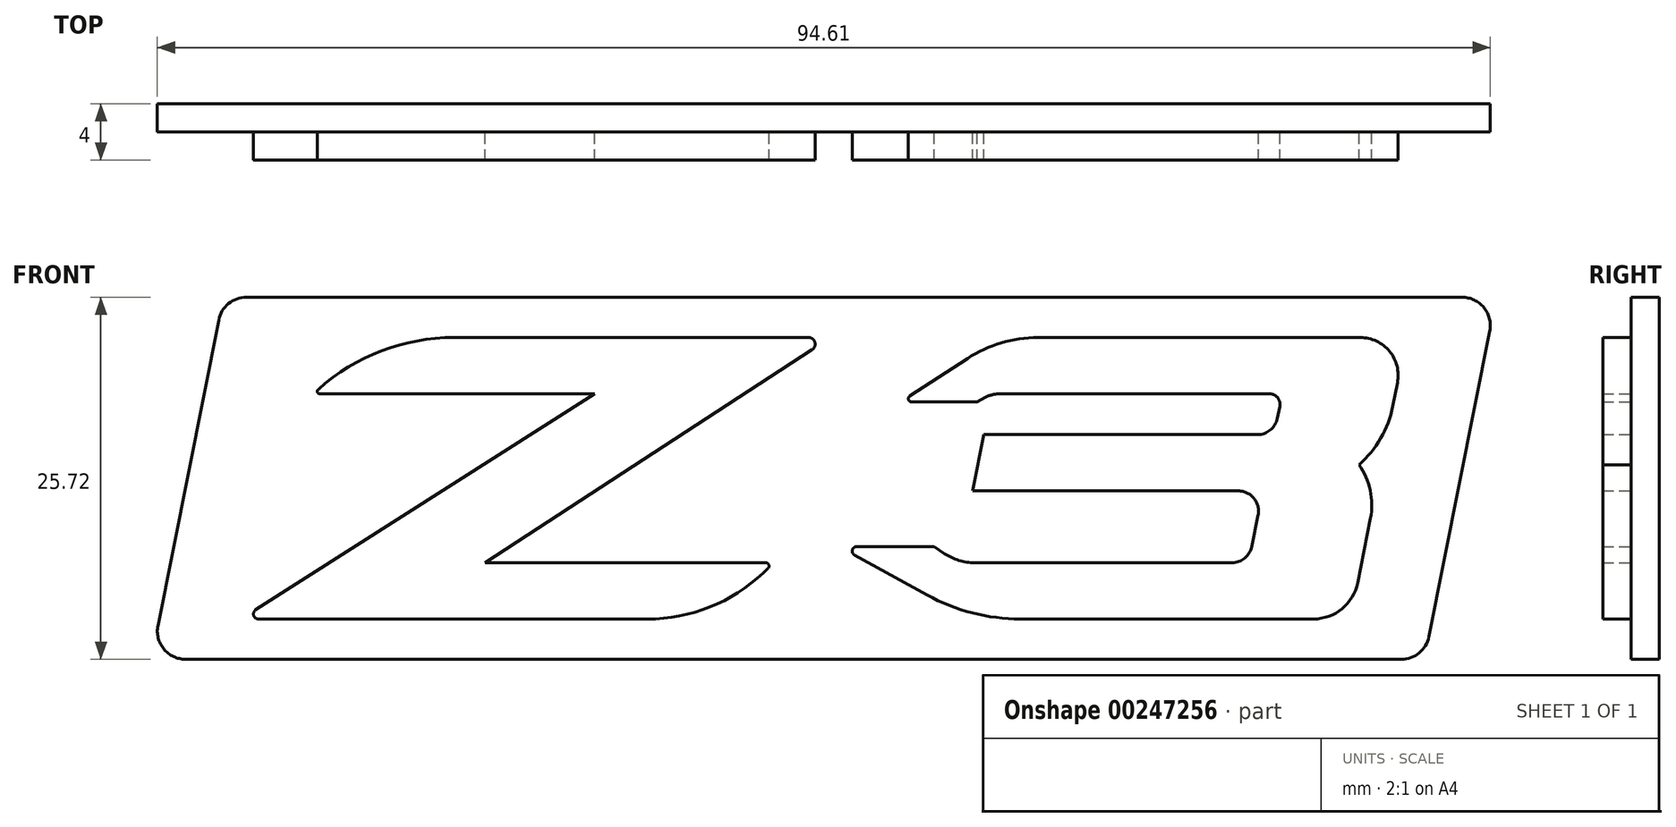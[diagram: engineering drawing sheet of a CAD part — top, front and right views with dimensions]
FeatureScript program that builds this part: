
annotation { "Feature Type Name" : "Feature", "Feature Type Description" : "" }
export const myFeature = defineFeature(function(context is Context, id is Id, definition is map)
    precondition{}
    {
        {
            var Q0;
            Q0=qCreatedBy(makeId("Front.planeOp"),FACE);
            var sketch = newSketch(context, id + "F0", { "sketchPlane" : qUnion([Q0])});
            skLineSegment(sketch, "E0", {"start": v(-146.44, 42.92) * mm, "end": v(151.69, 42.92) * mm, "construction": true});
            skLineSegment(sketch, "E1", {"start": v(-146.44, -27.08) * mm, "end": v(151.69, -27.08) * mm, "construction": true});
            skLineSegment(sketch, "E2", {"start": v(-146.44, 28.92) * mm, "end": v(151.69, 28.92) * mm, "construction": true});
            skLineSegment(sketch, "E3", {"start": v(-146.44, -13.08) * mm, "end": v(131.87, -13.08) * mm, "construction": true});
            skLineSegment(sketch, "E4", {"start": v(-142.86, -24.8) * mm, "end": v(-58.68, 28.92) * mm});
            skLineSegment(sketch, "E5", {"start": v(-58.68, 28.92) * mm, "end": v(-126.94, 28.92) * mm});
            skLineSegment(sketch, "E6", {"start": v(-127.34, 29.98) * mm, "end": v(-127.28, 30.04) * mm});
            skLineSegment(sketch, "E7", {"start": v(-93.58, 42.92) * mm, "end": v(-5.53, 42.92) * mm});
            skLineSegment(sketch, "E8", {"start": v(-4.63, 39.9) * mm, "end": v(-85.86, -13.08) * mm});
            skLineSegment(sketch, "E9", {"start": v(-85.86, -13.08) * mm, "end": v(-16.17, -13.08) * mm});
            skLineSegment(sketch, "E10", {"start": v(-15.6, -14.51) * mm, "end": v(-16.8, -15.65) * mm});
            skLineSegment(sketch, "E11", {"start": v(-45.51, -27.08) * mm, "end": v(-142.2, -27.08) * mm});
            skLineSegment(sketch, "E12", {"start": v(41.87, 28.92) * mm, "end": v(106.05, 28.92) * mm});
            skLineSegment(sketch, "E13", {"start": v(99.7, -13.08) * mm, "end": v(35.77, -13.08) * mm});
            skLineSegment(sketch, "E14", {"start": v(110.12, 18.76) * mm, "end": v(107.34, 4.76) * mm, "construction": true});
            skLineSegment(sketch, "E15", {"start": v(106.15, -1.2) * mm, "end": v(104.6, -9.06) * mm});
            skLineSegment(sketch, "E16", {"start": v(106.02, 18.76) * mm, "end": v(38, 18.76) * mm});
            skLineSegment(sketch, "E17", {"start": v(38, 18.76) * mm, "end": v(35.22, 4.76) * mm});
            skLineSegment(sketch, "E18", {"start": v(35.22, 4.76) * mm, "end": v(101.25, 4.76) * mm});
            skLineSegment(sketch, "E19", {"start": v(33.98, 37.72) * mm, "end": v(19.62, 28.35) * mm});
            skLineSegment(sketch, "E20", {"start": v(20.05, 26.92) * mm, "end": v(36.32, 26.92) * mm});
            skLineSegment(sketch, "E21", {"start": v(36.32, 26.92) * mm, "end": v(38.4, 28.04) * mm});
            skLineSegment(sketch, "E22", {"start": v(38, 18.76) * mm, "end": v(42.8, 42.92) * mm, "construction": true});
            skLineSegment(sketch, "E23", {"start": v(130.88, -18.05) * mm, "end": v(131.87, -13.08) * mm});
            skLineSegment(sketch, "E24", {"start": v(51.48, 42.92) * mm, "end": v(131.57, 42.92) * mm});
            skLineSegment(sketch, "E25", {"start": v(119.88, -27.08) * mm, "end": v(47.15, -27.08) * mm});
            skLineSegment(sketch, "E26", {"start": v(23.92, -21.1) * mm, "end": v(5.88, -11.14) * mm});
            skLineSegment(sketch, "E27", {"start": v(6.41, -9.08) * mm, "end": v(25.65, -9.08) * mm});
            skLineSegment(sketch, "E28", {"start": v(25.65, -9.08) * mm, "end": v(28.27, -10.82) * mm});
            skLineSegment(sketch, "E29", {"start": v(35.22, 4.76) * mm, "end": v(31.68, -13.08) * mm, "construction": true});
            skLineSegment(sketch, "E30", {"start": v(131.87, -13.08) * mm, "end": v(151.69, -13.08) * mm, "construction": true});
            skLineSegment(sketch, "E31", {"start": v(140.22, 28.92) * mm, "end": v(140.77, 31.7) * mm});
            skLineSegment(sketch, "E32", {"start": v(131.87, -13.08) * mm, "end": v(140.22, 28.92) * mm, "construction": true});
            skLineSegment(sketch, "E33", {"start": v(131.87, -13.08) * mm, "end": v(134.06, -2.07) * mm});
            skLineSegment(sketch, "E34", {"start": v(116.96, 18.76) * mm, "end": v(110.12, 18.76) * mm, "construction": true});
            skPoint(sketch, "E35.visualSharp", {"position": v(138.2, 18.76) * mm});
            skArc(sketch, "E35.filletArc", {"start": v(134.06, -2.07) * mm, "mid": v(134.02, 4.9) * mm, "end": v(131.26, 11.3) * mm});
            skLineSegment(sketch, "E36", {"start": v(140.22, 28.92) * mm, "end": v(139.6, 25.8) * mm});
            skLineSegment(sketch, "E37", {"start": v(113.97, 4.76) * mm, "end": v(107.34, 4.76) * mm, "construction": true});
            skPoint(sketch, "E38.visualSharp", {"position": v(135.42, 4.76) * mm});
            skArc(sketch, "E38.filletArc", {"start": v(113.97, 4.76) * mm, "mid": v(123.21, 6.45) * mm, "end": v(131.26, 11.3) * mm, "construction": true});
            skArc(sketch, "E39", {"start": v(131.26, 11.3) * mm, "mid": v(125.02, 16.79) * mm, "end": v(116.96, 18.76) * mm, "construction": true});
            skArc(sketch, "E40", {"start": v(131.26, 11.3) * mm, "mid": v(136.62, 17.87) * mm, "end": v(139.6, 25.8) * mm});
            skPoint(sketch, "E41.visualSharp", {"position": v(110.12, 18.76) * mm});
            skArc(sketch, "E41.filletArc", {"start": v(106.02, 18.76) * mm, "mid": v(109.2, 19.9) * mm, "end": v(110.92, 22.8) * mm});
            skPoint(sketch, "E42.visualSharp", {"position": v(107.34, 4.76) * mm});
            skArc(sketch, "E42.filletArc", {"start": v(106.15, -1.2) * mm, "mid": v(105.11, 2.94) * mm, "end": v(101.25, 4.76) * mm});
            skPoint(sketch, "E43.visualSharp", {"position": v(103.8, -13.08) * mm});
            skArc(sketch, "E43.filletArc", {"start": v(99.7, -13.08) * mm, "mid": v(102.86, -11.95) * mm, "end": v(104.6, -9.06) * mm});
            skPoint(sketch, "E44.visualSharp", {"position": v(143, 42.92) * mm});
            skArc(sketch, "E44.filletArc", {"start": v(140.77, 31.7) * mm, "mid": v(138.82, 39.49) * mm, "end": v(131.57, 42.92) * mm});
            skPoint(sketch, "E45.visualSharp", {"position": v(129.09, -27.08) * mm});
            skArc(sketch, "E45.filletArc", {"start": v(119.88, -27.08) * mm, "mid": v(127, -24.54) * mm, "end": v(130.88, -18.05) * mm});
            skPoint(sketch, "E46.visualSharp", {"position": v(34.76, -27.08) * mm});
            skArc(sketch, "E46.filletArc", {"start": v(23.92, -21.1) * mm, "mid": v(35.15, -25.56) * mm, "end": v(47.15, -27.08) * mm});
            skPoint(sketch, "E47.visualSharp", {"position": v(2.16, -9.08) * mm});
            skArc(sketch, "E47.filletArc", {"start": v(6.41, -9.08) * mm, "mid": v(5.35, -9.9) * mm, "end": v(5.88, -11.14) * mm});
            skPoint(sketch, "E48.visualSharp", {"position": v(31.68, -13.08) * mm});
            skArc(sketch, "E48.filletArc", {"start": v(28.27, -10.82) * mm, "mid": v(31.85, -12.5) * mm, "end": v(35.77, -13.08) * mm});
            skPoint(sketch, "E49.visualSharp", {"position": v(40.02, 28.92) * mm});
            skArc(sketch, "E49.filletArc", {"start": v(41.87, 28.92) * mm, "mid": v(40.08, 28.7) * mm, "end": v(38.4, 28.04) * mm});
            skPoint(sketch, "E50.visualSharp", {"position": v(17.42, 26.92) * mm});
            skArc(sketch, "E50.filletArc", {"start": v(19.62, 28.35) * mm, "mid": v(19.3, 27.47) * mm, "end": v(20.05, 26.92) * mm});
            skPoint(sketch, "E51.visualSharp", {"position": v(0, 42.92) * mm});
            skArc(sketch, "E51.filletArc", {"start": v(-4.63, 39.9) * mm, "mid": v(-3.95, 41.74) * mm, "end": v(-5.53, 42.92) * mm});
            skPoint(sketch, "E52.visualSharp", {"position": v(-28.88, -27.08) * mm});
            skArc(sketch, "E52.filletArc", {"start": v(-45.51, -27.08) * mm, "mid": v(-30.06, -24.12) * mm, "end": v(-16.8, -15.65) * mm});
            skPoint(sketch, "E53.visualSharp", {"position": v(-14.1, -13.08) * mm});
            skArc(sketch, "E53.filletArc", {"start": v(-15.6, -14.51) * mm, "mid": v(-15.4, -13.6) * mm, "end": v(-16.17, -13.08) * mm});
            skPoint(sketch, "E54.visualSharp", {"position": v(-146.44, -27.08) * mm});
            skArc(sketch, "E54.filletArc", {"start": v(-142.86, -24.8) * mm, "mid": v(-143.39, -26.2) * mm, "end": v(-142.2, -27.08) * mm});
            skPoint(sketch, "E55.visualSharp", {"position": v(-112.89, 42.92) * mm});
            skArc(sketch, "E55.filletArc", {"start": v(-93.58, 42.92) * mm, "mid": v(-111.62, 39.59) * mm, "end": v(-127.28, 30.04) * mm});
            skPoint(sketch, "E56.visualSharp", {"position": v(-128.53, 28.92) * mm});
            skArc(sketch, "E56.filletArc", {"start": v(-127.34, 29.98) * mm, "mid": v(-127.5, 29.3) * mm, "end": v(-126.94, 28.92) * mm});
            skLineSegment(sketch, "E57", {"start": v(110.92, 22.8) * mm, "end": v(111.53, 25.85) * mm});
            skLineSegment(sketch, "E58", {"start": v(109.02, 28.92) * mm, "end": v(106.05, 28.92) * mm});
            skPoint(sketch, "E59.visualSharp", {"position": v(112.14, 28.92) * mm});
            skArc(sketch, "E59.filletArc", {"start": v(111.53, 25.85) * mm, "mid": v(111, 27.98) * mm, "end": v(109.02, 28.92) * mm});
            skPoint(sketch, "E60.visualSharp", {"position": v(41.95, 42.92) * mm});
            skArc(sketch, "E60.filletArc", {"start": v(51.48, 42.92) * mm, "mid": v(42.35, 41.59) * mm, "end": v(33.98, 37.72) * mm});
            skLineSegment(sketch, "E61", {"start": v(165.38, 52.92) * mm, "end": v(147.5, -37.08) * mm});
            skLineSegment(sketch, "E62", {"start": v(147.5, -37.08) * mm, "end": v(-168.81, -37.08) * mm});
            skLineSegment(sketch, "E63", {"start": v(-168.81, -37.08) * mm, "end": v(-150.93, 52.92) * mm});
            skLineSegment(sketch, "E64", {"start": v(-150.93, 52.92) * mm, "end": v(165.38, 52.92) * mm});
            skSolve(sketch);
        }
        {
            var Q0;
            Q0 = qSketchRegion(id + "F0", true);
            var Q1;
            Q1=makeQuery(id+"F0.imprint","IMPRINT",FACE,{"disambiguationData":[TD([[makeQuery(id+"F0.imprint","IMPRINT",EDGE,{"derivedFrom":sQuery(id+"F0.wireOp",EDGE,"E4")}),-1.0]])]});
            var Q2;
            Q2=makeQuery(id+"F0.imprint","IMPRINT",FACE,{"disambiguationData":[TD([[makeQuery(id+"F0.imprint","IMPRINT",EDGE,{"derivedFrom":sQuery(id+"F0.wireOp",EDGE,"E12")}),1.0]])]});
            extrude(context, id + "F1", {"entities" : qUnion([Q0, Q1, Q2]), "oppositeDirection" : true, "depth" : 7 * mm});
        }
        {
            var Q0;
            Q0=makeQuery(id+"F0.imprint","IMPRINT",FACE,{"disambiguationData":[TD([[makeQuery(id+"F0.imprint","IMPRINT",EDGE,{"derivedFrom":sQuery(id+"F0.wireOp",EDGE,"E4")}),-1.0]])]});
            var Q1;
            Q1=makeQuery(id+"F0.imprint","IMPRINT",FACE,{"disambiguationData":[TD([[makeQuery(id+"F0.imprint","IMPRINT",EDGE,{"derivedFrom":sQuery(id+"F0.wireOp",EDGE,"E12")}),1.0]])]});
            extrude(context, id + "F2", {"entities" : qUnion([Q0, Q1]), "operationType" : NewBodyOperationType.ADD, "depth" : 7 * mm});
        }
        {
            var Q0;
            Q0=makeQuery(id+"F1.opExtrude","SWEPT_BODY",BODY,{"disambiguationData":[OSD([sQuery(id+"F0.wireOp",EDGE,"E61"),sQuery(id+"F0.wireOp",EDGE,"E62"),sQuery(id+"F0.wireOp",EDGE,"E63"),sQuery(id+"F0.wireOp",EDGE,"E64")])]});
            var Q1;
            Q1=qCreatedBy(makeId("Origin.pointOp"),VERTEX);
            transform(context, id + "F3", {"entities" : qUnion([Q0]), "transformType" : TransformType.SCALE_UNIFORMLY, "scale" : 2 / 7, "scalePoint" : qUnion([Q1]), "makeCopy" : false});
        }
        {
            var Q0;
            Q0=makeQuery(id+"F1.opExtrude","SWEPT_EDGE",EDGE,{"disambiguationData":[OSD([sQuery(id+"F0.wireOp",EDGE,"E62"),sQuery(id+"F0.wireOp",EDGE,"E63")])]});
            var Q1;
            Q1=makeQuery(id+"F1.opExtrude","SWEPT_EDGE",EDGE,{"disambiguationData":[OSD([sQuery(id+"F0.wireOp",EDGE,"E63"),sQuery(id+"F0.wireOp",EDGE,"E64")])]});
            var Q2;
            Q2=makeQuery(id+"F1.opExtrude","SWEPT_EDGE",EDGE,{"disambiguationData":[OSD([sQuery(id+"F0.wireOp",EDGE,"E61"),sQuery(id+"F0.wireOp",EDGE,"E64")])]});
            var Q3;
            Q3=makeQuery(id+"F1.opExtrude","SWEPT_EDGE",EDGE,{"disambiguationData":[OSD([sQuery(id+"F0.wireOp",EDGE,"E61"),sQuery(id+"F0.wireOp",EDGE,"E62")])]});
            fillet(context, id + "F4", {"entities" : qUnion([Q0, Q1, Q2, Q3]), "radius" : 2 * mm, "tangentPropagation" : true, "allowEdgeOverflow" : false});
        }
    });
